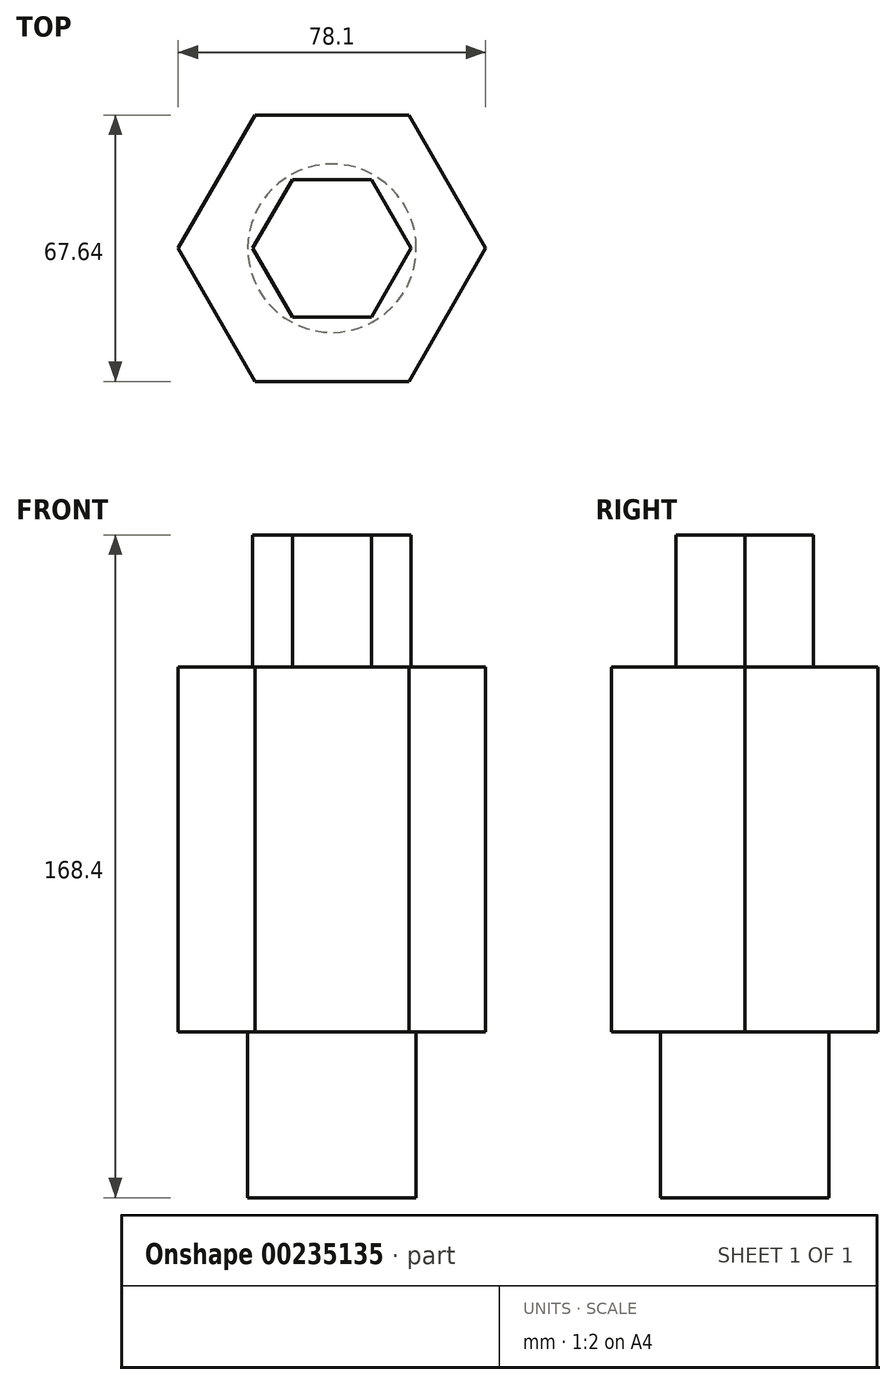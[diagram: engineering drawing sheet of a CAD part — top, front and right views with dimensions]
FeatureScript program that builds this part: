
annotation { "Feature Type Name" : "Feature", "Feature Type Description" : "" }
export const myFeature = defineFeature(function(context is Context, id is Id, definition is map)
    precondition{}
    {
        {
            var Q0;
            Q0=qCreatedBy(makeId("Top.planeOp"),FACE);
            var sketch = newSketch(context, id + "F0", { "sketchPlane" : qUnion([Q0])});
            skCircle(sketch, "E0.cCircle", {"center": v(0, 0) * mm, "radius": 33.82 * mm, "construction": true});
            skLineSegment(sketch, "E0.0", {"start": v(-19.53, 33.82) * mm, "end": v(19.53, 33.82) * mm});
            skLineSegment(sketch, "E0.1", {"start": v(19.53, 33.82) * mm, "end": v(39.05, 0) * mm});
            skLineSegment(sketch, "E0.2", {"start": v(39.05, 0) * mm, "end": v(19.53, -33.82) * mm});
            skLineSegment(sketch, "E0.3", {"start": v(19.53, -33.82) * mm, "end": v(-19.53, -33.82) * mm});
            skLineSegment(sketch, "E0.4", {"start": v(-19.53, -33.82) * mm, "end": v(-39.05, 0) * mm});
            skLineSegment(sketch, "E0.5", {"start": v(-39.05, 0) * mm, "end": v(-19.53, 33.82) * mm});
            skPoint(sketch, "E0.0.midPoint", {"position": v(0, 33.82) * mm});
            skSolve(sketch);
        }
        {
            var Q0;
            Q0=makeQuery(id+"F0.imprint","IMPRINT",FACE,{"disambiguationData":[TD([[makeQuery(id+"F0.imprint","IMPRINT",EDGE,{"derivedFrom":sQuery(id+"F0.wireOp",EDGE,"E0.0")}),-1.0]])]});
            extrude(context, id + "F1", {"entities" : qUnion([Q0]), "depth" : 92.7 * mm});
        }
        {
            var Q0;
            Q0=makeQuery(id+"F1.opExtrude","CAP_FACE",FACE,{"disambiguationData":[OSD([sQuery(id+"F0.wireOp",EDGE,"E0.0"),sQuery(id+"F0.wireOp",EDGE,"E0.1"),sQuery(id+"F0.wireOp",EDGE,"E0.2"),sQuery(id+"F0.wireOp",EDGE,"E0.3"),sQuery(id+"F0.wireOp",EDGE,"E0.4"),sQuery(id+"F0.wireOp",EDGE,"E0.5")])],"isStart":false});
            var sketch = newSketch(context, id + "F2", { "sketchPlane" : qUnion([Q0])});
            skCircle(sketch, "E1.cCircle", {"center": v(0, 0) * mm, "radius": 17.43 * mm, "construction": true});
            skLineSegment(sketch, "E1.0", {"start": v(-10.06, 17.43) * mm, "end": v(10.06, 17.43) * mm});
            skLineSegment(sketch, "E1.1", {"start": v(10.06, 17.43) * mm, "end": v(20.13, 0) * mm});
            skLineSegment(sketch, "E1.2", {"start": v(20.13, 0) * mm, "end": v(10.06, -17.43) * mm});
            skLineSegment(sketch, "E1.3", {"start": v(10.06, -17.43) * mm, "end": v(-10.06, -17.43) * mm});
            skLineSegment(sketch, "E1.4", {"start": v(-10.06, -17.43) * mm, "end": v(-20.13, 0) * mm});
            skLineSegment(sketch, "E1.5", {"start": v(-20.13, 0) * mm, "end": v(-10.06, 17.43) * mm});
            skPoint(sketch, "E1.0.midPoint", {"position": v(0, 17.43) * mm});
            skSolve(sketch);
        }
        {
            var Q0;
            Q0=makeQuery(id+"F2.imprint","IMPRINT",FACE,{"disambiguationData":[TD([[makeQuery(id+"F2.imprint","IMPRINT",EDGE,{"derivedFrom":sQuery(id+"F2.wireOp",EDGE,"E1.0")}),-1.0]])]});
            extrude(context, id + "F3", {"entities" : qUnion([Q0]), "operationType" : NewBodyOperationType.ADD, "depth" : 33.53 * mm});
        }
        {
            var Q0;
            Q0=makeQuery(id+"F1.opExtrude","CAP_FACE",FACE,{"disambiguationData":[OSD([sQuery(id+"F0.wireOp",EDGE,"E0.0"),sQuery(id+"F0.wireOp",EDGE,"E0.1"),sQuery(id+"F0.wireOp",EDGE,"E0.2"),sQuery(id+"F0.wireOp",EDGE,"E0.3"),sQuery(id+"F0.wireOp",EDGE,"E0.4"),sQuery(id+"F0.wireOp",EDGE,"E0.5")])],"isStart":true});
            var sketch = newSketch(context, id + "F4", { "sketchPlane" : qUnion([Q0])});
            skCircle(sketch, "E2", {"center": v(0, 0) * mm, "radius": 21.4 * mm});
            skSolve(sketch);
        }
        {
            var Q0;
            Q0=makeQuery(id+"F4.imprint","IMPRINT",FACE,{"disambiguationData":[TD([[makeQuery(id+"F4.imprint","IMPRINT",EDGE,{"derivedFrom":sQuery(id+"F4.wireOp",EDGE,"E2")}),1.0]])]});
            extrude(context, id + "F5", {"entities" : qUnion([Q0]), "operationType" : NewBodyOperationType.ADD, "depth" : 42.16 * mm});
        }
    });
